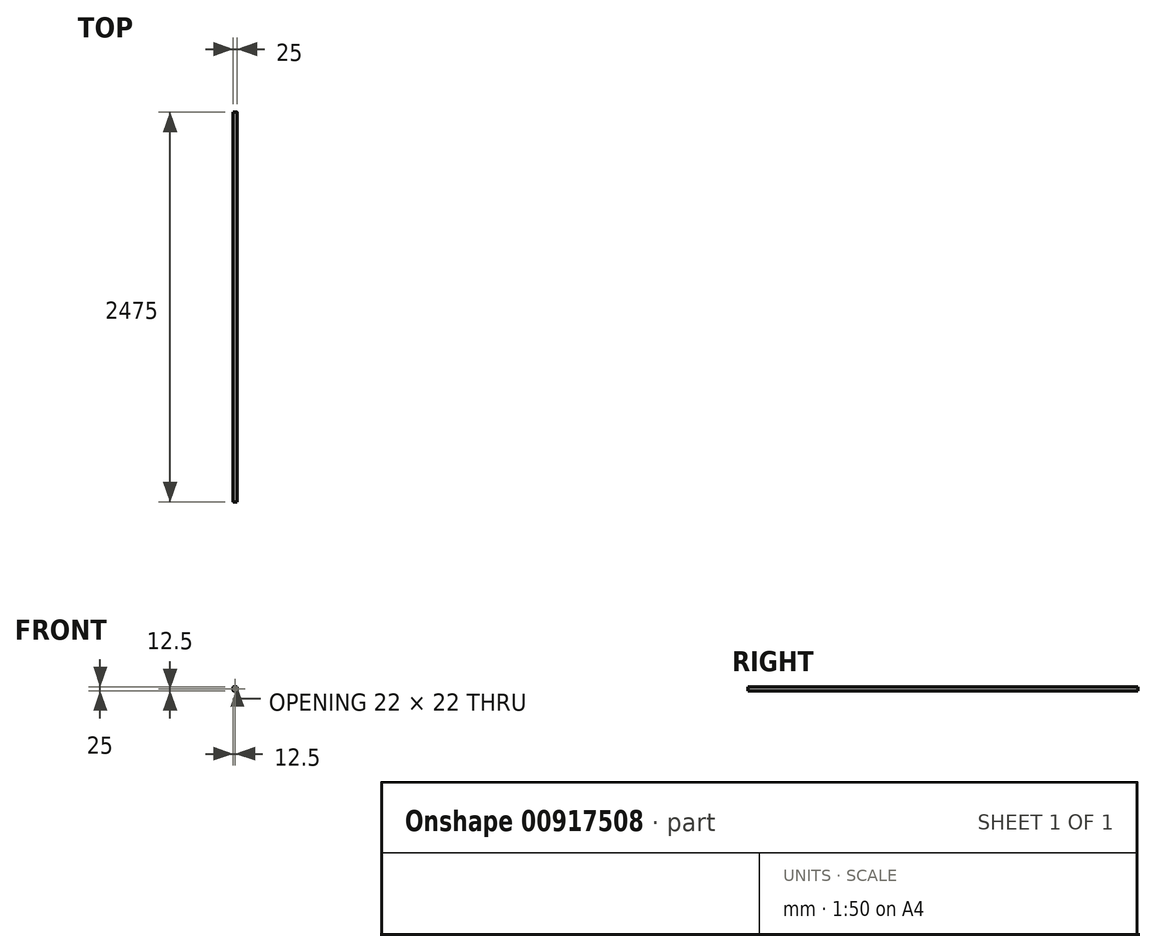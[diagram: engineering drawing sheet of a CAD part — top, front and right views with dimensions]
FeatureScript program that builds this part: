
annotation { "Feature Type Name" : "Feature", "Feature Type Description" : "" }
export const myFeature = defineFeature(function(context is Context, id is Id, definition is map)
    precondition{}
    {
        {
            var Q0;
            Q0=qCreatedBy(makeId("Front.planeOp"),FACE);
            var sketch = newSketch(context, id + "F0", { "sketchPlane" : qUnion([Q0])});
            skLineSegment(sketch, "E0.bottom", {"start": v(10, 12.5) * mm, "end": v(-10, 12.5) * mm});
            skLineSegment(sketch, "E0.top", {"start": v(10, -12.5) * mm, "end": v(-10, -12.5) * mm});
            skLineSegment(sketch, "E0.left", {"start": v(12.5, 10) * mm, "end": v(12.5, -10) * mm});
            skLineSegment(sketch, "E0.right", {"start": v(-12.5, 10) * mm, "end": v(-12.5, -10) * mm});
            skPoint(sketch, "E0.middle", {"position": v(0, 0) * mm});
            skPoint(sketch, "E1.visualSharp", {"position": v(12.5, 12.5) * mm});
            skArc(sketch, "E1.filletArc", {"start": v(12.5, 10) * mm, "mid": v(11.77, 11.77) * mm, "end": v(10, 12.5) * mm});
            skPoint(sketch, "E2.visualSharp", {"position": v(12.5, -12.5) * mm});
            skArc(sketch, "E2.filletArc", {"start": v(10, -12.5) * mm, "mid": v(11.77, -11.77) * mm, "end": v(12.5, -10) * mm});
            skPoint(sketch, "E3.visualSharp", {"position": v(-12.5, -12.5) * mm});
            skArc(sketch, "E3.filletArc", {"start": v(-12.5, -10) * mm, "mid": v(-11.77, -11.77) * mm, "end": v(-10, -12.5) * mm});
            skPoint(sketch, "E4.visualSharp", {"position": v(-12.5, 12.5) * mm});
            skArc(sketch, "E4.filletArc", {"start": v(-10, 12.5) * mm, "mid": v(-11.77, 11.77) * mm, "end": v(-12.5, 10) * mm});
            skLineSegment(sketch, "E5.0", {"start": v(11, 10) * mm, "end": v(11, -10) * mm});
            skLineSegment(sketch, "E5.1", {"start": v(10, 11) * mm, "end": v(-10, 11) * mm});
            skLineSegment(sketch, "E5.2", {"start": v(-11, 10) * mm, "end": v(-11, -10) * mm});
            skLineSegment(sketch, "E5.3", {"start": v(10, -11) * mm, "end": v(-10, -11) * mm});
            skPoint(sketch, "E6.visualSharp", {"position": v(-11, 11) * mm});
            skArc(sketch, "E6.filletArc", {"start": v(-10, 11) * mm, "mid": v(-10.7, 10.7) * mm, "end": v(-11, 10) * mm});
            skPoint(sketch, "E7.visualSharp", {"position": v(-11, -11) * mm});
            skArc(sketch, "E7.filletArc", {"start": v(-11, -10) * mm, "mid": v(-10.7, -10.7) * mm, "end": v(-10, -11) * mm});
            skPoint(sketch, "E8.visualSharp", {"position": v(11, -11) * mm});
            skArc(sketch, "E8.filletArc", {"start": v(10, -11) * mm, "mid": v(10.7, -10.7) * mm, "end": v(11, -10) * mm});
            skPoint(sketch, "E9.visualSharp", {"position": v(11, 11) * mm});
            skArc(sketch, "E9.filletArc", {"start": v(11, 10) * mm, "mid": v(10.7, 10.7) * mm, "end": v(10, 11) * mm});
            skSolve(sketch);
        }
        {
            var Q0;
            Q0=qSketchRegion(id+"F0",true);
            extrude(context, id + "F1", {"entities" : qUnion([Q0]), "depth" : 2475 * mm, "offsetDistance" : 25 * mm, "symmetric" : true});
        }
    });
